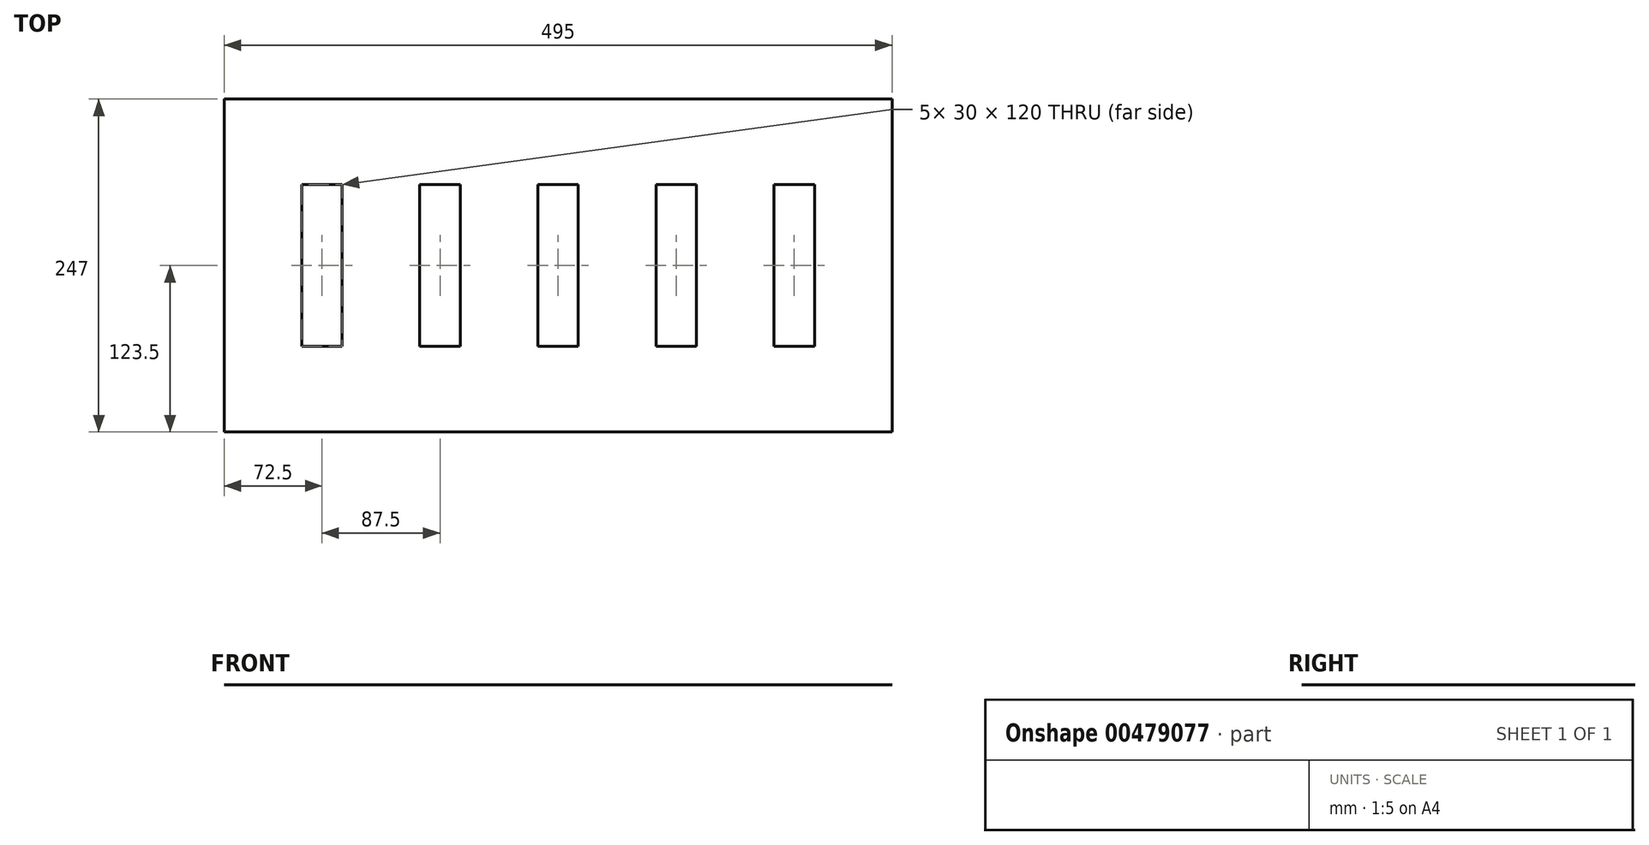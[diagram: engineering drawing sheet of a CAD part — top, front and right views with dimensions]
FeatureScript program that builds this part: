
annotation { "Feature Type Name" : "Feature", "Feature Type Description" : "" }
export const myFeature = defineFeature(function(context is Context, id is Id, definition is map)
    precondition{}
    {
        {
            var Q0;
            Q0=qCreatedBy(makeId("Top.planeOp"),FACE);
            var sketch = newSketch(context, id + "F0", { "sketchPlane" : qUnion([Q0])});
            skLineSegment(sketch, "E0.bottom", {"start": v(-247.5, 123.5) * mm, "end": v(247.5, 123.5) * mm});
            skLineSegment(sketch, "E0.top", {"start": v(-247.5, -123.5) * mm, "end": v(247.5, -123.5) * mm});
            skLineSegment(sketch, "E0.left", {"start": v(-247.5, 123.5) * mm, "end": v(-247.5, -123.5) * mm});
            skLineSegment(sketch, "E0.right", {"start": v(247.5, 123.5) * mm, "end": v(247.5, -123.5) * mm});
            skLineSegment(sketch, "E1.bottom", {"start": v(-190, 60) * mm, "end": v(-160, 60) * mm});
            skLineSegment(sketch, "E1.top", {"start": v(-190, -60) * mm, "end": v(-160, -60) * mm});
            skLineSegment(sketch, "E1.left", {"start": v(-190, 60) * mm, "end": v(-190, -60) * mm});
            skLineSegment(sketch, "E1.right", {"start": v(-160, 60) * mm, "end": v(-160, -60) * mm});
            skLineSegment(sketch, "E2.bottom", {"start": v(-102.5, 60) * mm, "end": v(-72.5, 60) * mm});
            skLineSegment(sketch, "E2.top", {"start": v(-102.5, -60) * mm, "end": v(-72.5, -60) * mm});
            skLineSegment(sketch, "E2.left", {"start": v(-102.5, 60) * mm, "end": v(-102.5, -60) * mm});
            skLineSegment(sketch, "E2.right", {"start": v(-72.5, 60) * mm, "end": v(-72.5, -60) * mm});
            skLineSegment(sketch, "E3.bottom", {"start": v(-15, 60) * mm, "end": v(15, 60) * mm});
            skLineSegment(sketch, "E3.top", {"start": v(-15, -60) * mm, "end": v(15, -60) * mm});
            skLineSegment(sketch, "E3.left", {"start": v(-15, 60) * mm, "end": v(-15, -60) * mm});
            skLineSegment(sketch, "E3.right", {"start": v(15, 60) * mm, "end": v(15, -60) * mm});
            skLineSegment(sketch, "E4.bottom", {"start": v(72.5, 60) * mm, "end": v(102.5, 60) * mm});
            skLineSegment(sketch, "E4.top", {"start": v(72.5, -60) * mm, "end": v(102.5, -60) * mm});
            skLineSegment(sketch, "E4.left", {"start": v(72.5, 60) * mm, "end": v(72.5, -60) * mm});
            skLineSegment(sketch, "E4.right", {"start": v(102.5, 60) * mm, "end": v(102.5, -60) * mm});
            skLineSegment(sketch, "E5.bottom", {"start": v(160, 60) * mm, "end": v(190, 60) * mm});
            skLineSegment(sketch, "E5.top", {"start": v(160, -60) * mm, "end": v(190, -60) * mm});
            skLineSegment(sketch, "E5.left", {"start": v(160, 60) * mm, "end": v(160, -60) * mm});
            skLineSegment(sketch, "E5.right", {"start": v(190, 60) * mm, "end": v(190, -60) * mm});
            skPoint(sketch, "E6.end.orphan", {"position": v(-247.5, 0) * mm});
            skPoint(sketch, "E6.start.orphan", {"position": v(-190, 0) * mm});
            skPoint(sketch, "E7.end.orphan", {"position": v(-102.5, 0) * mm});
            skPoint(sketch, "E7.start.orphan", {"position": v(-160, 0) * mm});
            skPoint(sketch, "E8.end.orphan", {"position": v(-15, 0) * mm});
            skPoint(sketch, "E8.start.orphan", {"position": v(-72.5, 0) * mm});
            skPoint(sketch, "E9.end.orphan", {"position": v(72.5, 0) * mm});
            skPoint(sketch, "E9.start.orphan", {"position": v(15, 0) * mm});
            skPoint(sketch, "E10.end.orphan", {"position": v(160, 0) * mm});
            skPoint(sketch, "E10.start.orphan", {"position": v(102.5, 0) * mm});
            skPoint(sketch, "E11.end.orphan", {"position": v(247.5, 0) * mm});
            skPoint(sketch, "E11.start.orphan", {"position": v(190, 0) * mm});
            skLineSegment(sketch, "E12", {"start": v(-247.5, 0) * mm, "end": v(-190, 0) * mm});
            skLineSegment(sketch, "E13", {"start": v(-160, 0) * mm, "end": v(-102.5, 0) * mm});
            skLineSegment(sketch, "E14", {"start": v(-72.5, 0) * mm, "end": v(-15, 0) * mm});
            skLineSegment(sketch, "E15", {"start": v(15, 0) * mm, "end": v(72.5, 0) * mm});
            skLineSegment(sketch, "E16", {"start": v(102.5, 0) * mm, "end": v(160, 0) * mm});
            skLineSegment(sketch, "E17", {"start": v(190, 0) * mm, "end": v(247.5, 0) * mm});
            skPoint(sketch, "E18.end.orphan", {"position": v(0, 0) * mm});
            skPoint(sketch, "E19.orphan", {"position": v(0, -60) * mm});
            skPoint(sketch, "E20.start.orphan", {"position": v(0, 60) * mm});
            skSolve(sketch);
        }
        {
            var Q0;
            Q0=makeQuery(id+"F0.imprint","IMPRINT",FACE,{"disambiguationData":[TD([[makeQuery(id+"F0.imprint","IMPRINT",EDGE,{"derivedFrom":sQuery(id+"F0.wireOp",EDGE,"E0.bottom")}),-1.0]])]});
            var Q1;
            {var subQ16=sQuery(id+"F0.wireOp",EDGE,"E0.top");Q1=makeQuery(id+"F0.imprint","IMPRINT",FACE,{"disambiguationData":[TD([[makeQuery(id+"F0.imprint","IMPRINT",EDGE,{"derivedFrom":subQ16}),1.0]])]});}
            extrude(context, id + "F1", {"entities" : qUnion([Q0, Q1]), "oppositeDirection" : true, "depth" : 1 / 203.2 * mm});
        }
    });
